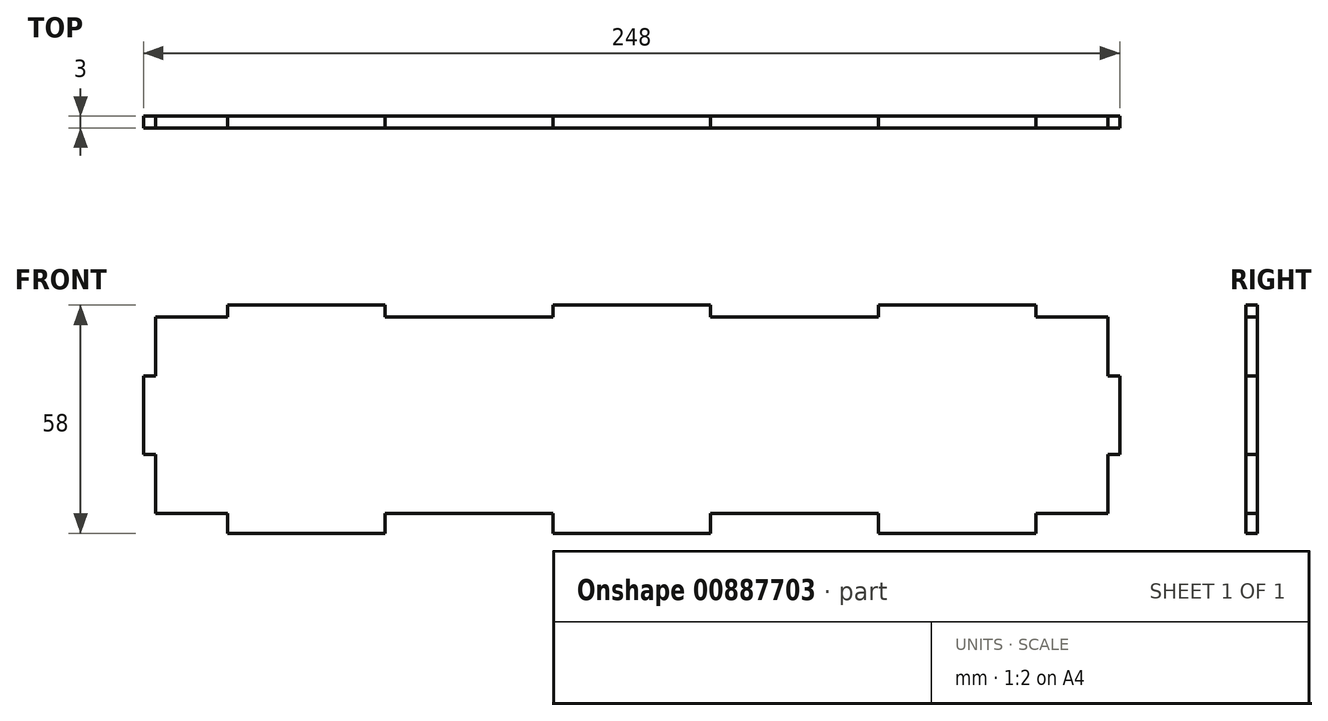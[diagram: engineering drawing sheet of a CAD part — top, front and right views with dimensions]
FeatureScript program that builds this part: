
annotation { "Feature Type Name" : "Feature", "Feature Type Description" : "" }
export const myFeature = defineFeature(function(context is Context, id is Id, definition is map)
    precondition{}
    {
        {
            var Q0;
            Q0=qCreatedBy(makeId("Front.planeOp"),FACE);
            var sketch = newSketch(context, id + "F0", { "sketchPlane" : qUnion([Q0])});
            skLineSegment(sketch, "E0.bottom", {"start": v(121, -25) * mm, "end": v(102.67, -25) * mm});
            skLineSegment(sketch, "E0.top", {"start": v(121, 25) * mm, "end": v(102.67, 25) * mm});
            skLineSegment(sketch, "E0.left", {"start": v(121, -25) * mm, "end": v(121, -10) * mm});
            skLineSegment(sketch, "E0.right", {"start": v(-121, -25) * mm, "end": v(-121, -10) * mm});
            skPoint(sketch, "E0.middle", {"position": v(0, 0) * mm});
            skLineSegment(sketch, "E1", {"start": v(-102.67, -25) * mm, "end": v(-102.67, -30) * mm});
            skLineSegment(sketch, "E2", {"start": v(-102.67, -30) * mm, "end": v(-62.67, -30) * mm});
            skLineSegment(sketch, "E3", {"start": v(-62.67, -30) * mm, "end": v(-62.67, -25) * mm});
            skLineSegment(sketch, "E4", {"start": v(-20, -25) * mm, "end": v(-20, -30) * mm});
            skLineSegment(sketch, "E5", {"start": v(-20, -30) * mm, "end": v(20, -30) * mm});
            skLineSegment(sketch, "E6", {"start": v(20, -30) * mm, "end": v(20, -25) * mm});
            skLineSegment(sketch, "E7.MirrorCS", {"start": v(62.67, -30) * mm, "end": v(62.67, -25) * mm});
            skLineSegment(sketch, "E8.MirrorCS", {"start": v(102.67, -30) * mm, "end": v(62.67, -30) * mm});
            skLineSegment(sketch, "E9.MirrorCS", {"start": v(102.67, -25) * mm, "end": v(102.67, -30) * mm});
            skLineSegment(sketch, "E10.trimOffspring", {"start": v(-102.67, -25) * mm, "end": v(-121, -25) * mm});
            skLineSegment(sketch, "E11.trimOffspring", {"start": v(-20, -25) * mm, "end": v(-62.67, -25) * mm});
            skLineSegment(sketch, "E12.trimOffspring", {"start": v(62.67, -25) * mm, "end": v(20, -25) * mm});
            skLineSegment(sketch, "E13", {"start": v(-102.67, 25) * mm, "end": v(-102.67, 28) * mm});
            skLineSegment(sketch, "E14", {"start": v(-102.67, 28) * mm, "end": v(-62.67, 28) * mm});
            skLineSegment(sketch, "E15", {"start": v(-62.67, 28) * mm, "end": v(-62.67, 25) * mm});
            skLineSegment(sketch, "E16", {"start": v(-20, 25) * mm, "end": v(-20, 28) * mm});
            skLineSegment(sketch, "E17", {"start": v(-20, 28) * mm, "end": v(20, 28) * mm});
            skLineSegment(sketch, "E18", {"start": v(20, 28) * mm, "end": v(20, 25) * mm});
            skLineSegment(sketch, "E19.trimOffspring", {"start": v(-102.67, 25) * mm, "end": v(-121, 25) * mm});
            skLineSegment(sketch, "E20.trimOffspring", {"start": v(-20, 25) * mm, "end": v(-62.67, 25) * mm});
            skLineSegment(sketch, "E21.MirrorCS", {"start": v(102.67, 28) * mm, "end": v(62.67, 28) * mm});
            skLineSegment(sketch, "E22.MirrorCS", {"start": v(62.67, 28) * mm, "end": v(62.67, 25) * mm});
            skLineSegment(sketch, "E23.MirrorCS", {"start": v(102.67, 25) * mm, "end": v(102.67, 28) * mm});
            skLineSegment(sketch, "E24", {"start": v(-121, 10) * mm, "end": v(-124, 10) * mm});
            skLineSegment(sketch, "E25", {"start": v(-124, 10) * mm, "end": v(-124, -10) * mm});
            skLineSegment(sketch, "E26", {"start": v(-124, -10) * mm, "end": v(-121, -10) * mm});
            skLineSegment(sketch, "E27.MirrorCS", {"start": v(124, 10) * mm, "end": v(124, -10) * mm});
            skLineSegment(sketch, "E28.MirrorCS", {"start": v(124, -10) * mm, "end": v(121, -10) * mm});
            skLineSegment(sketch, "E29.trimOffspring", {"start": v(-121, 10) * mm, "end": v(-121, 25) * mm});
            skLineSegment(sketch, "E30.MirrorCS", {"start": v(121, 10) * mm, "end": v(124, 10) * mm});
            skLineSegment(sketch, "E31.trimOffspring", {"start": v(121, 10) * mm, "end": v(121, 25) * mm});
            skLineSegment(sketch, "E32.trimOffspring", {"start": v(62.67, 25) * mm, "end": v(20, 25) * mm});
            skSolve(sketch);
        }
        {
            var Q0;
            Q0=makeQuery(id+"F0.imprint","IMPRINT",FACE,{"disambiguationData":[TD([[makeQuery(id+"F0.imprint","IMPRINT",EDGE,{"derivedFrom":sQuery(id+"F0.wireOp",EDGE,"E0.bottom")}),-1.0]])]});
            extrude(context, id + "F1", {"entities" : qUnion([Q0]), "depth" : 3 * mm, "offsetDistance" : 25 * mm});
        }
    });
